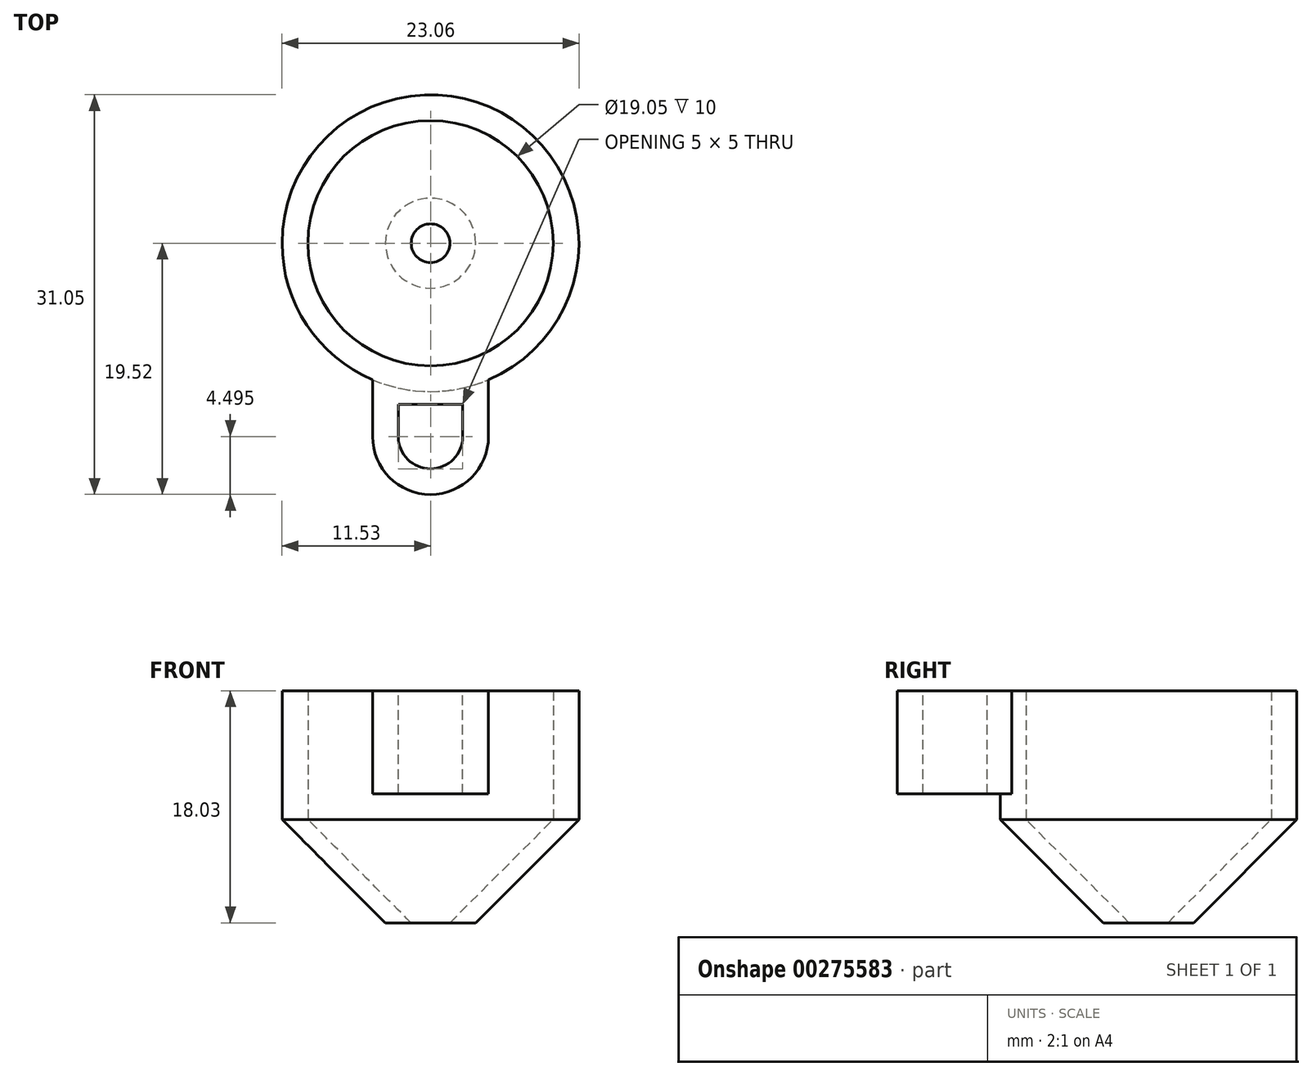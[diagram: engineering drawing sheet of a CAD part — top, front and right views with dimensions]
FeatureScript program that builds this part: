
annotation { "Feature Type Name" : "Feature", "Feature Type Description" : "" }
export const myFeature = defineFeature(function(context is Context, id is Id, definition is map)
    precondition{}
    {
        {
            var Q0;
            Q0=qCreatedBy(makeId("Right.planeOp"),FACE);
            var sketch = newSketch(context, id + "F0", { "sketchPlane" : qUnion([Q0])});
            skLineSegment(sketch, "E0", {"start": v(0, 0) * mm, "end": v(0, 20.37) * mm, "construction": true});
            skLineSegment(sketch, "E1", {"start": v(9.52, 8.03) * mm, "end": v(1.5, 0) * mm});
            skLineSegment(sketch, "E2", {"start": v(1.5, 0) * mm, "end": v(3.5, 0) * mm});
            skLineSegment(sketch, "E3", {"start": v(3.5, 0) * mm, "end": v(11.52, 8.03) * mm});
            skLineSegment(sketch, "E4", {"start": v(11.52, 8.03) * mm, "end": v(11.52, 18.03) * mm});
            skLineSegment(sketch, "E5", {"start": v(11.52, 18.03) * mm, "end": v(9.52, 18.03) * mm});
            skLineSegment(sketch, "E6", {"start": v(9.52, 18.03) * mm, "end": v(9.53, 8.03) * mm});
            skSolve(sketch);
        }
        {
            var Q0;
            Q0 = qSketchRegion(id + "F0", true);
            var Q1;
            Q1=sQuery(id+"F0.wireOp",EDGE,"E0");
            revolve(context, id + "F1", {"entities" : qUnion([Q0]), "axis" : qUnion([Q1]), "revolveType" : RevolveType.FULL});
        }
        {
            var Q0;
            Q0=makeQuery(id+"F1.opRevolve","SWEPT_FACE",FACE,{"disambiguationData":[OSD([sQuery(id+"F0.wireOp",EDGE,"E5")])]});
            var sketch = newSketch(context, id + "F2", { "sketchPlane" : qUnion([Q0])});
            skLineSegment(sketch, "E7", {"start": v(0, 0) * mm, "end": v(0, -11.52) * mm, "construction": true});
            skLineSegment(sketch, "E8", {"start": v(-2.5, -12.52) * mm, "end": v(-2.5, -15.03) * mm});
            skArc(sketch, "E9", {"start": v(-2.5, -15.03) * mm, "mid": v(0, -17.53) * mm, "end": v(2.5, -15.03) * mm});
            skLineSegment(sketch, "E10.MirrorCS", {"start": v(2.5, -12.52) * mm, "end": v(2.5, -15.03) * mm});
            skLineSegment(sketch, "E11", {"start": v(-2.5, -12.52) * mm, "end": v(2.5, -12.52) * mm});
            skLineSegment(sketch, "E12", {"start": v(-4.5, -10.61) * mm, "end": v(-4.5, -15.03) * mm});
            skArc(sketch, "E13", {"start": v(-4.5, -15.03) * mm, "mid": v(0, -19.52) * mm, "end": v(4.5, -15.02) * mm});
            skLineSegment(sketch, "E14", {"start": v(4.5, -15.02) * mm, "end": v(4.5, -10.61) * mm});
            skArc(sketch, "E15.0", {"start": v(-4.5, -10.61) * mm, "mid": v(0, -11.53) * mm, "end": v(4.5, -10.61) * mm});
            skSolve(sketch);
        }
        {
            var Q0;
            Q0 = qSketchRegion(id + "F2", true);
            extrude(context, id + "F3", {"entities" : qUnion([Q0]), "operationType" : NewBodyOperationType.ADD, "oppositeDirection" : true, "depth" : 8 * mm});
        }
    });
